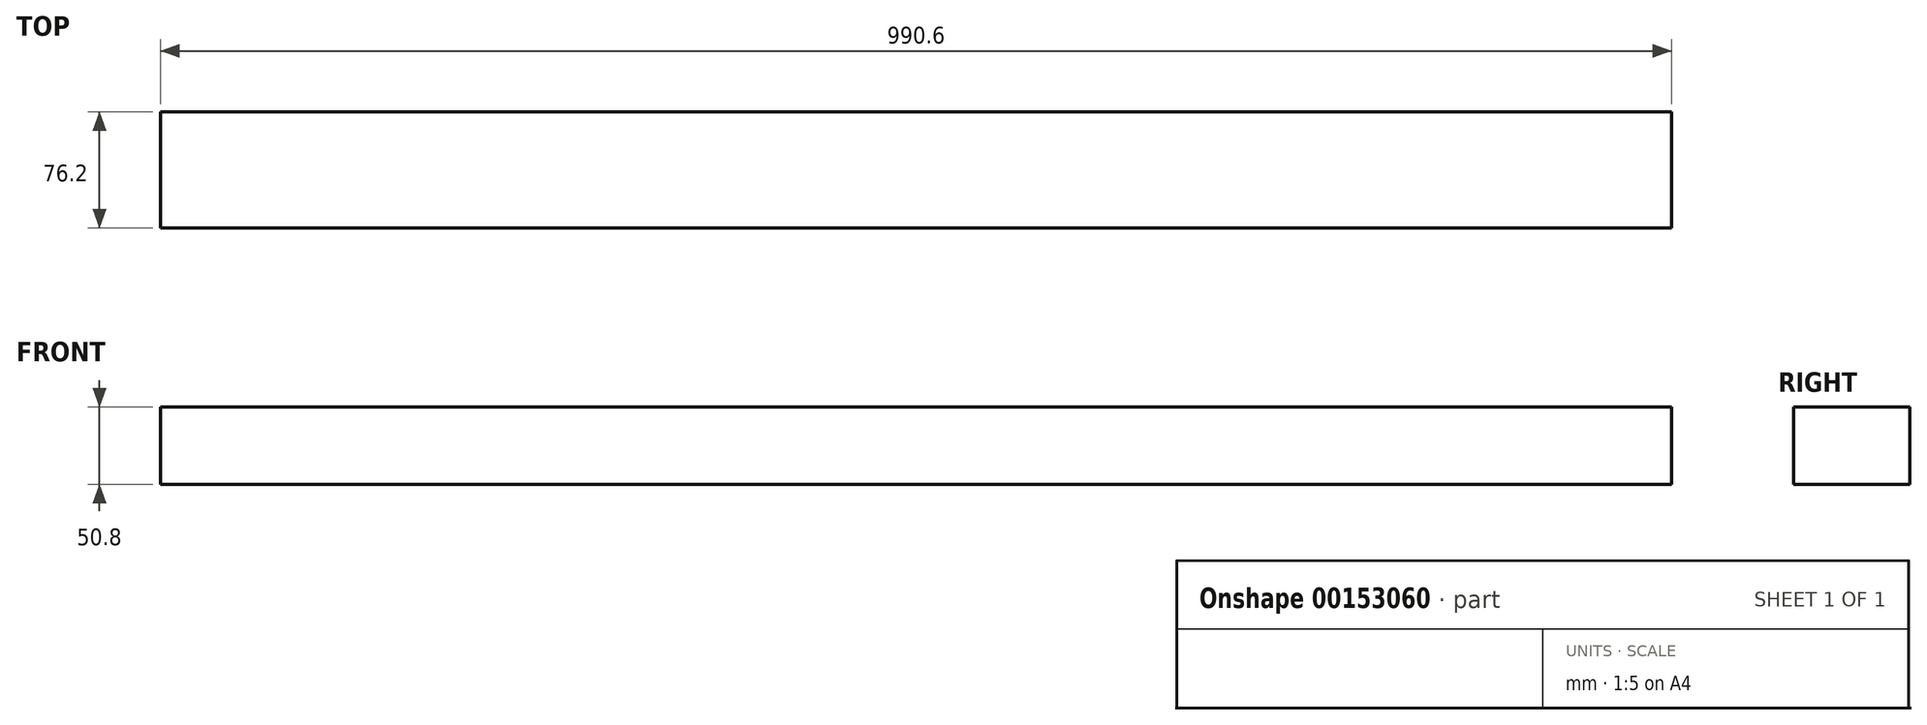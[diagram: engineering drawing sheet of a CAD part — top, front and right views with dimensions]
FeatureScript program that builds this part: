
annotation { "Feature Type Name" : "Feature", "Feature Type Description" : "" }
export const myFeature = defineFeature(function(context is Context, id is Id, definition is map)
    precondition{}
    {
        {
            var Q0;
            Q0=qCreatedBy(makeId("Top.planeOp"),FACE);
            var sketch = newSketch(context, id + "F0", { "sketchPlane" : qUnion([Q0])});
            skLineSegment(sketch, "E0.bottom", {"start": v(0, 0) * mm, "end": v(990.6, 0) * mm});
            skLineSegment(sketch, "E0.top", {"start": v(0, 76.2) * mm, "end": v(990.6, 76.2) * mm});
            skLineSegment(sketch, "E0.left", {"start": v(0, 0) * mm, "end": v(0, 76.2) * mm});
            skLineSegment(sketch, "E0.right", {"start": v(990.6, 0) * mm, "end": v(990.6, 76.2) * mm});
            skSolve(sketch);
        }
        {
            var Q0;
            Q0=makeQuery(id+"F0.imprint","IMPRINT",FACE,{"disambiguationData":[TD([[makeQuery(id+"F0.imprint","IMPRINT",EDGE,{"derivedFrom":sQuery(id+"F0.wireOp",EDGE,"E0.bottom")}),1.0]])]});
            extrude(context, id + "F1", {"entities" : qUnion([Q0]), "depth" : 50.8 * mm});
        }
    });
